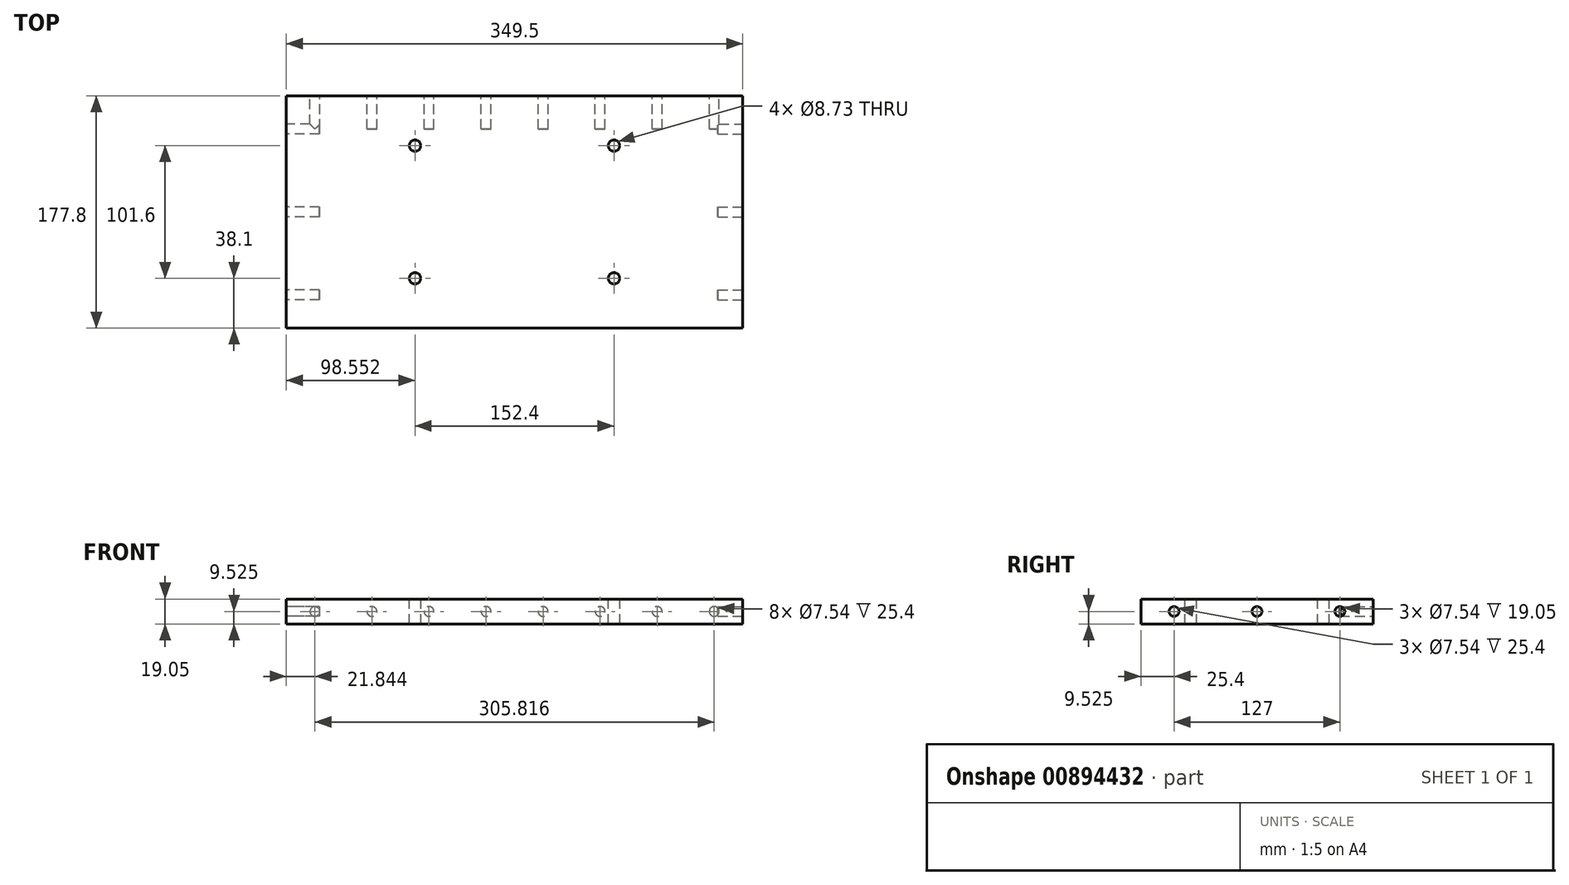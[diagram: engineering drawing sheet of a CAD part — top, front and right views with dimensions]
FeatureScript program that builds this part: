
annotation { "Feature Type Name" : "Feature", "Feature Type Description" : "" }
export const myFeature = defineFeature(function(context is Context, id is Id, definition is map)
    precondition{}
    {
        {
            var Q0;
            Q0=qCreatedBy(makeId("Top.planeOp"),FACE);
            var sketch = newSketch(context, id + "F0", { "sketchPlane" : qUnion([Q0])});
            skLineSegment(sketch, "E0.bottom", {"start": v(0, 0) * mm, "end": v(349.5, 0) * mm});
            skLineSegment(sketch, "E0.top", {"start": v(0, 177.8) * mm, "end": v(349.5, 177.8) * mm});
            skLineSegment(sketch, "E0.left", {"start": v(0, 0) * mm, "end": v(0, 177.8) * mm});
            skLineSegment(sketch, "E0.right", {"start": v(349.5, 0) * mm, "end": v(349.5, 177.8) * mm});
            skSolve(sketch);
        }
        {
            var Q0;
            Q0=makeQuery(id+"F0.imprint","IMPRINT",FACE,{"disambiguationData":[TD([[makeQuery(id+"F0.imprint","IMPRINT",EDGE,{"derivedFrom":sQuery(id+"F0.wireOp",EDGE,"E0.bottom")}),1.0]])]});
            extrude(context, id + "F1", {"entities" : qUnion([Q0]), "depth" : 19.05 * mm, "offsetDistance" : 25.4 * mm});
        }
        {
            var Q0;
            Q0=makeQuery(id+"F1.opExtrude","SWEPT_FACE",FACE,{"disambiguationData":[OSD([sQuery(id+"F0.wireOp",EDGE,"E0.right")])]});
            var sketch = newSketch(context, id + "F2", { "sketchPlane" : qUnion([Q0])});
            skCircle(sketch, "E1", {"center": v(88.9, 9.53) * mm, "radius": 3.77 * mm});
            skCircle(sketch, "E2", {"center": v(25.4, 9.53) * mm, "radius": 3.77 * mm});
            skCircle(sketch, "E3", {"center": v(152.4, 9.53) * mm, "radius": 3.77 * mm});
            skSolve(sketch);
        }
        {
            var Q0;
            Q0=qSketchRegion(id+"F2",true);
            extrude(context, id + "F3", {"entities" : qUnion([Q0]), "operationType" : NewBodyOperationType.REMOVE, "oppositeDirection" : true, "depth" : 19.05 * mm, "offsetDistance" : 25.4 * mm});
        }
        {
            var Q0;
            Q0=makeQuery(id+"F1.opExtrude","SWEPT_FACE",FACE,{"disambiguationData":[OSD([sQuery(id+"F0.wireOp",EDGE,"E0.left")])]});
            var sketch = newSketch(context, id + "F4", { "sketchPlane" : qUnion([Q0])});
            skCircle(sketch, "E4", {"center": v(-88.9, 9.53) * mm, "radius": 3.77 * mm});
            skCircle(sketch, "E5", {"center": v(-25.4, 9.53) * mm, "radius": 3.77 * mm});
            skCircle(sketch, "E6", {"center": v(-152.4, 9.53) * mm, "radius": 3.77 * mm});
            skSolve(sketch);
        }
        {
            var Q0;
            Q0=qSketchRegion(id+"F4",true);
            extrude(context, id + "F5", {"entities" : qUnion([Q0]), "operationType" : NewBodyOperationType.REMOVE, "oppositeDirection" : true, "depth" : 25.4 * mm, "offsetDistance" : 25.4 * mm});
        }
        {
            var Q0;
            Q0=makeQuery(id+"F1.opExtrude","CAP_FACE",FACE,{"disambiguationData":[OSD([sQuery(id+"F0.wireOp",EDGE,"E0.bottom"),sQuery(id+"F0.wireOp",EDGE,"E0.top"),sQuery(id+"F0.wireOp",EDGE,"E0.left"),sQuery(id+"F0.wireOp",EDGE,"E0.right")])],"isStart":false});
            var sketch = newSketch(context, id + "F6", { "sketchPlane" : qUnion([Q0])});
            skCircle(sketch, "E7", {"center": v(98.55, 139.7) * mm, "radius": 4.37 * mm});
            skCircle(sketch, "E8", {"center": v(98.55, 38.1) * mm, "radius": 4.37 * mm});
            skCircle(sketch, "E9", {"center": v(250.95, 139.7) * mm, "radius": 4.37 * mm});
            skCircle(sketch, "E10", {"center": v(250.95, 38.1) * mm, "radius": 4.37 * mm});
            skLineSegment(sketch, "E11", {"start": v(174.75, 177.8) * mm, "end": v(174.75, -22) * mm});
            skSolve(sketch);
        }
        {
            var Q0;
            Q0=qSketchRegion(id+"F6",true);
            extrude(context, id + "F7", {"entities" : qUnion([Q0]), "operationType" : NewBodyOperationType.REMOVE, "oppositeDirection" : true, "depth" : 25.4 * mm, "offsetDistance" : 25.4 * mm});
        }
        {
            var Q0;
            Q0=makeQuery(id+"F1.opExtrude","SWEPT_FACE",FACE,{"disambiguationData":[OSD([sQuery(id+"F0.wireOp",EDGE,"E0.top")])]});
            var sketch = newSketch(context, id + "F8", { "sketchPlane" : qUnion([Q0])});
            skCircle(sketch, "E12", {"center": v(-21.84, 9.53) * mm, "radius": 3.77 * mm});
            skCircle(sketch, "E13.1.0.0", {"center": v(-65.53, 9.53) * mm, "radius": 3.77 * mm});
            skCircle(sketch, "E13.2.0.0", {"center": v(-109.22, 9.53) * mm, "radius": 3.77 * mm});
            skCircle(sketch, "E13.3.0.0", {"center": v(-152.9, 9.53) * mm, "radius": 3.77 * mm});
            skCircle(sketch, "E13.4.0.0", {"center": v(-196.6, 9.53) * mm, "radius": 3.77 * mm});
            skCircle(sketch, "E13.5.0.0", {"center": v(-240.28, 9.53) * mm, "radius": 3.77 * mm});
            skLineSegment(sketch, "E13.direction1", {"start": v(-21.84, 9.53) * mm, "end": v(-65.53, 9.53) * mm, "construction": true});
            skCircle(sketch, "E14.0.6.0", {"center": v(-283.97, 9.53) * mm, "radius": 3.77 * mm});
            skCircle(sketch, "E14.0.7.0", {"center": v(-327.66, 9.53) * mm, "radius": 3.77 * mm});
            skSolve(sketch);
        }
        {
            var Q0;
            Q0=qSketchRegion(id+"F8",true);
            extrude(context, id + "F9", {"entities" : qUnion([Q0]), "operationType" : NewBodyOperationType.REMOVE, "oppositeDirection" : true, "depth" : 25.4 * mm, "offsetDistance" : 25.4 * mm});
        }
    });
